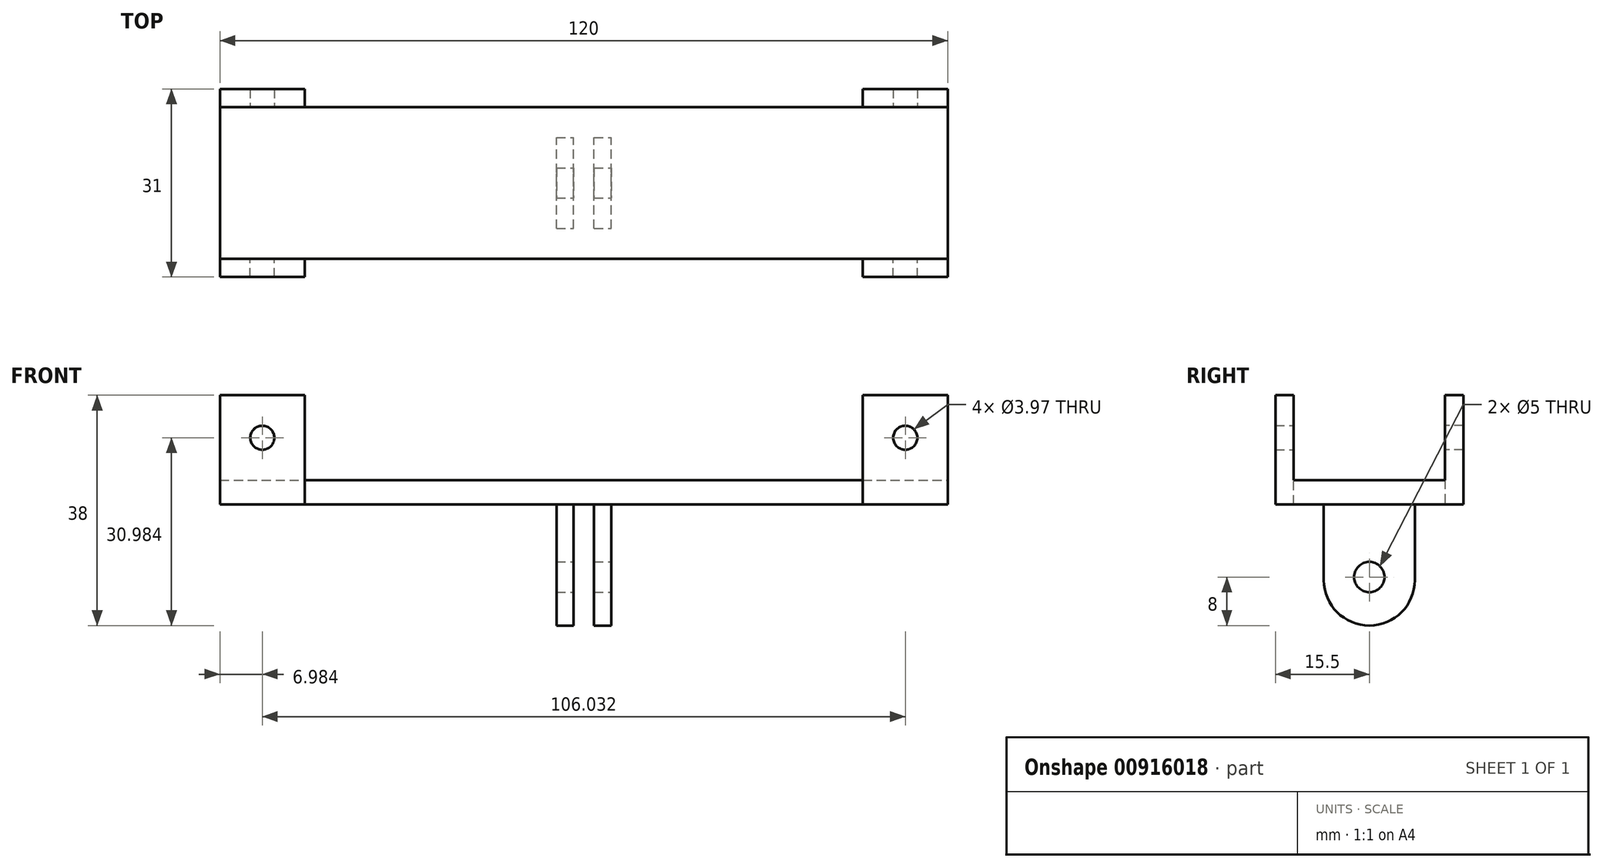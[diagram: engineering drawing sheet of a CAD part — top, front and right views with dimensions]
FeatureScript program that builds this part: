
annotation { "Feature Type Name" : "Feature", "Feature Type Description" : "" }
export const myFeature = defineFeature(function(context is Context, id is Id, definition is map)
    precondition{}
    {
        {
            var Q0;
            Q0=qCreatedBy(makeId("Front.planeOp"),FACE);
            var sketch = newSketch(context, id + "F0", { "sketchPlane" : qUnion([Q0])});
            skLineSegment(sketch, "E0.bottom", {"start": v(1.7, 10) * mm, "end": v(4.5, 10) * mm});
            skLineSegment(sketch, "E0.top", {"start": v(1.7, -10) * mm, "end": v(4.5, -10) * mm});
            skLineSegment(sketch, "E0.left", {"start": v(1.7, 10) * mm, "end": v(1.7, -10) * mm});
            skLineSegment(sketch, "E0.right", {"start": v(4.5, 10) * mm, "end": v(4.5, -10) * mm});
            skPoint(sketch, "E0.middle", {"position": v(3.1, 0) * mm});
            skLineSegment(sketch, "E1.bottom", {"start": v(-4.5, 10) * mm, "end": v(-1.7, 10) * mm});
            skLineSegment(sketch, "E1.top", {"start": v(-4.5, -10) * mm, "end": v(-1.7, -10) * mm});
            skLineSegment(sketch, "E1.left", {"start": v(-4.5, 10) * mm, "end": v(-4.5, -10) * mm});
            skLineSegment(sketch, "E1.right", {"start": v(-1.7, 10) * mm, "end": v(-1.7, -10) * mm});
            skPoint(sketch, "E1.middle", {"position": v(-3.1, 0) * mm});
            skLineSegment(sketch, "E2.bottom", {"start": v(-60, 14) * mm, "end": v(60, 14) * mm});
            skLineSegment(sketch, "E2.top", {"start": v(-60, 10) * mm, "end": v(60, 10) * mm});
            skLineSegment(sketch, "E2.left", {"start": v(-60, 14) * mm, "end": v(-60, 10) * mm});
            skLineSegment(sketch, "E2.right", {"start": v(60, 14) * mm, "end": v(60, 10) * mm});
            skPoint(sketch, "E2.middle", {"position": v(0, 12) * mm});
            skSolve(sketch);
        }
        {
            var Q0;
            Q0=makeQuery(id+"F0.imprint","IMPRINT",FACE,{"disambiguationData":[TD([[makeQuery(id+"F0.imprint","IMPRINT",EDGE,{"derivedFrom":sQuery(id+"F0.wireOp",EDGE,"E1.top")}),1.0]])]});
            var Q1;
            Q1=makeQuery(id+"F0.imprint","IMPRINT",FACE,{"disambiguationData":[TD([[makeQuery(id+"F0.imprint","IMPRINT",EDGE,{"derivedFrom":sQuery(id+"F0.wireOp",EDGE,"E0.top")}),1.0]])]});
            extrude(context, id + "F1", {"entities" : qUnion([Q0, Q1]), "endBound" : BoundingType.SYMMETRIC, "depth" : 15 * mm, "offsetDistance" : 25 * mm});
        }
        {
            var Q0;
            Q0=makeQuery(id+"F1.opExtrude","SWEPT_FACE",FACE,{"disambiguationData":[OSD([sQuery(id+"F0.wireOp",EDGE,"E0.right")])]});
            cPlane(context, id + "F2", {"entities" : qUnion([Q0]), "cplaneType" : CPlaneType.OFFSET, "offset" : 0 * mm, "width" : 150 * mm, "height" : 150 * mm});
        }
        {
            var Q0;
            Q0=qCreatedBy(id+"F2.planeOp",FACE);
            var sketch = newSketch(context, id + "F3", { "sketchPlane" : qUnion([Q0])});
            skCircle(sketch, "E3", {"center": v(0, -2) * mm, "radius": 2.5 * mm});
            skSolve(sketch);
        }
        {
            var Q0;
            Q0=makeQuery(id+"F3.imprint","IMPRINT",FACE,{"disambiguationData":[TD([[makeQuery(id+"F3.imprint","IMPRINT",EDGE,{"derivedFrom":sQuery(id+"F3.wireOp",EDGE,"E3")}),1.0]])]});
            extrude(context, id + "F4", {"entities" : qUnion([Q0]), "operationType" : NewBodyOperationType.REMOVE, "endBound" : BoundingType.THROUGH_ALL, "oppositeDirection" : true, "depth" : 9 * mm, "offsetDistance" : 25 * mm});
        }
        {
            var Q0;
            Q0=makeQuery(id+"F1.opExtrude","CAP_EDGE",EDGE,{"disambiguationData":[OSD([sQuery(id+"F0.wireOp",EDGE,"E0.top")])],"isStart":false});
            var Q1;
            Q1=makeQuery(id+"F1.opExtrude","CAP_EDGE",EDGE,{"disambiguationData":[OSD([sQuery(id+"F0.wireOp",EDGE,"E1.top")])],"isStart":false});
            var Q2;
            Q2=makeQuery(id+"F1.opExtrude","CAP_EDGE",EDGE,{"disambiguationData":[OSD([sQuery(id+"F0.wireOp",EDGE,"E0.top")])],"isStart":true});
            var Q3;
            Q3=makeQuery(id+"F1.opExtrude","CAP_EDGE",EDGE,{"disambiguationData":[OSD([sQuery(id+"F0.wireOp",EDGE,"E1.top")])],"isStart":true});
            fillet(context, id + "F5", {"entities" : qUnion([Q0, Q1, Q2, Q3]), "radius" : 7.5 * mm, "tangentPropagation" : true, "allowEdgeOverflow" : false});
        }
        {
            var Q0;
            Q0=makeQuery(id+"F0.imprint","IMPRINT",FACE,{"disambiguationData":[TD([[makeQuery(id+"F0.imprint","IMPRINT",EDGE,{"derivedFrom":sQuery(id+"F0.wireOp",EDGE,"E2.bottom")}),-1.0]])]});
            extrude(context, id + "F6", {"entities" : qUnion([Q0]), "endBound" : BoundingType.SYMMETRIC, "depth" : 25 * mm, "offsetDistance" : 25 * mm});
        }
        {
            var Q0;
            Q0=makeQuery(id+"F6.opExtrude","CAP_FACE",FACE,{"disambiguationData":[OSD([sQuery(id+"F0.wireOp",EDGE,"E2.bottom"),sQuery(id+"F0.wireOp",EDGE,"E2.top"),sQuery(id+"F0.wireOp",EDGE,"E2.left"),sQuery(id+"F0.wireOp",EDGE,"E2.right"),sQuery(id+"F0.wireOp",EDGE,"LS6c8k6B-SqiU-ch4w-d8yS-Ls4rduuZiFJG.bottom"),sQuery(id+"F0.wireOp",EDGE,"1939846d-28db-450c-8804-b2f24aab8243.left")])],"isStart":false});
            cPlane(context, id + "F7", {"entities" : qUnion([Q0]), "cplaneType" : CPlaneType.OFFSET, "offset" : 0 * mm, "width" : 150 * mm, "height" : 150 * mm});
        }
        {
            var Q0;
            Q0=qCreatedBy(id+"F7.planeOp",FACE);
            var sketch = newSketch(context, id + "F8", { "sketchPlane" : qUnion([Q0])});
            skLineSegment(sketch, "E4.bottom", {"start": v(-60, 10) * mm, "end": v(-46, 10) * mm});
            skLineSegment(sketch, "E4.top", {"start": v(-60, 28) * mm, "end": v(-46, 28) * mm});
            skLineSegment(sketch, "E4.left", {"start": v(-60, 10) * mm, "end": v(-60, 28) * mm});
            skLineSegment(sketch, "E4.right", {"start": v(-46, 10) * mm, "end": v(-46, 28) * mm});
            skCircle(sketch, "E5", {"center": v(-53.02, 20.98) * mm, "radius": 1.98 * mm});
            skLineSegment(sketch, "E6.MirrorCS", {"start": v(46, 10) * mm, "end": v(46, 28) * mm});
            skLineSegment(sketch, "E7.MirrorCS", {"start": v(60, 10) * mm, "end": v(46, 10) * mm});
            skCircle(sketch, "E8.MirrorC", {"center": v(53.02, 20.98) * mm, "radius": 1.98 * mm});
            skLineSegment(sketch, "E9.MirrorCS", {"start": v(60, 28) * mm, "end": v(46, 28) * mm});
            skLineSegment(sketch, "E10.MirrorCS", {"start": v(60, 10) * mm, "end": v(60, 28) * mm});
            skSolve(sketch);
        }
        {
            var Q0;
            Q0 = qSketchRegion(id + "F8", true);
            extrude(context, id + "F9", {"entities" : qUnion([Q0]), "operationType" : NewBodyOperationType.ADD, "depth" : 3 * mm, "offsetDistance" : 25 * mm});
        }
        {
            var Q0;
            Q0=qCreatedBy(id+"F7.planeOp",FACE);
            cPlane(context, id + "F10", {"entities" : qUnion([Q0]), "cplaneType" : CPlaneType.OFFSET, "offset" : 25 * mm, "oppositeDirection" : true, "width" : 150 * mm, "height" : 150 * mm});
        }
        {
            var Q0;
            Q0=qCreatedBy(id+"F10.planeOp",FACE);
            var sketch = newSketch(context, id + "F11", { "sketchPlane" : qUnion([Q0])});
            skLineSegment(sketch, "E11.bottom", {"start": v(60, 28) * mm, "end": v(46, 28) * mm});
            skLineSegment(sketch, "E11.top", {"start": v(60, 10) * mm, "end": v(46, 10) * mm});
            skLineSegment(sketch, "E11.left", {"start": v(60, 28) * mm, "end": v(60, 10) * mm});
            skLineSegment(sketch, "E11.right", {"start": v(46, 28) * mm, "end": v(46, 10) * mm});
            skCircle(sketch, "E12", {"center": v(53.02, 20.98) * mm, "radius": 1.98 * mm});
            skLineSegment(sketch, "E13.MirrorCS", {"start": v(-60, 10) * mm, "end": v(-46, 10) * mm});
            skCircle(sketch, "E14.MirrorC", {"center": v(-53.02, 20.98) * mm, "radius": 1.98 * mm});
            skLineSegment(sketch, "E15.MirrorCS", {"start": v(-46, 28) * mm, "end": v(-46, 10) * mm});
            skLineSegment(sketch, "E16.MirrorCS", {"start": v(-60, 28) * mm, "end": v(-60, 10) * mm});
            skLineSegment(sketch, "E17.MirrorCS", {"start": v(-60, 28) * mm, "end": v(-46, 28) * mm});
            skSolve(sketch);
        }
        {
            var Q0;
            Q0=makeQuery(id+"F11.imprint","IMPRINT",FACE,{"disambiguationData":[TD([[makeQuery(id+"F11.imprint","IMPRINT",EDGE,{"derivedFrom":sQuery(id+"F11.wireOp",EDGE,"E11.bottom")}),1.0]])]});
            var Q1;
            Q1=makeQuery(id+"F11.imprint","IMPRINT",FACE,{"disambiguationData":[TD([[makeQuery(id+"F11.imprint","IMPRINT",EDGE,{"derivedFrom":sQuery(id+"F11.wireOp",EDGE,"E13.MirrorCS")}),1.0]])]});
            extrude(context, id + "F12", {"entities" : qUnion([Q0, Q1]), "operationType" : NewBodyOperationType.ADD, "depth" : -3 * mm, "offsetDistance" : 25 * mm});
        }
    });
